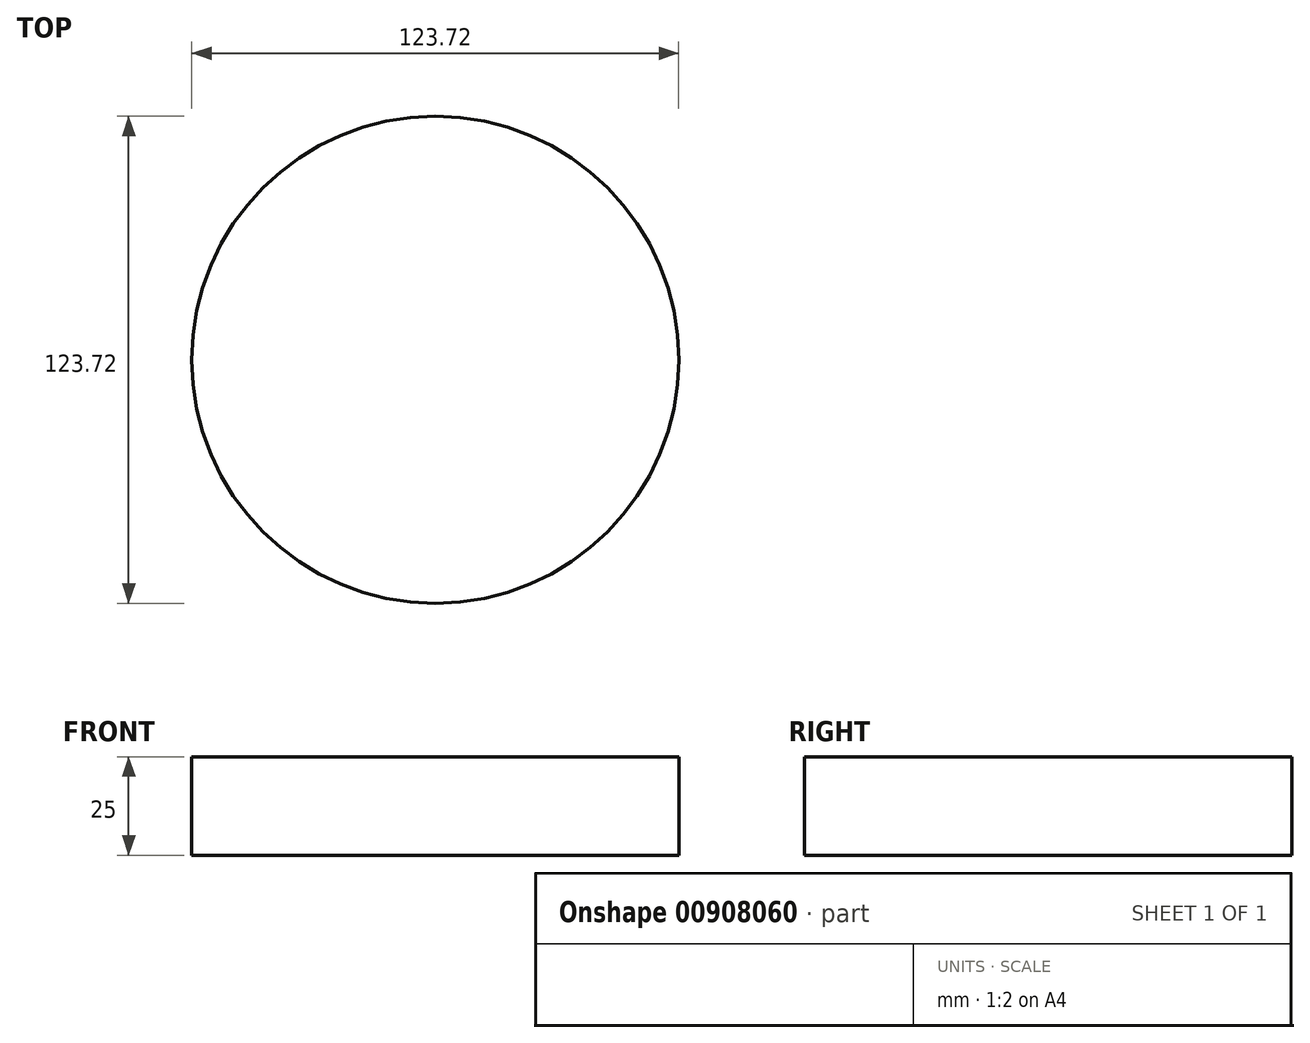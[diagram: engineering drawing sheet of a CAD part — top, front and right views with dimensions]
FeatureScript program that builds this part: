
annotation { "Feature Type Name" : "Feature", "Feature Type Description" : "" }
export const myFeature = defineFeature(function(context is Context, id is Id, definition is map)
    precondition{}
    {
        {
            var Q0;
            Q0=qCreatedBy(makeId("Top.planeOp"),FACE);
            var sketch = newSketch(context, id + "F0", { "sketchPlane" : qUnion([Q0])});
            skCircle(sketch, "E0", {"center": v(0, 0) * mm, "radius": 61.86 * mm});
            skSolve(sketch);
        }
        {
            var Q0;
            Q0=makeQuery(id+"F0.imprint","IMPRINT",FACE,{"disambiguationData":[TD([[makeQuery(id+"F0.imprint","IMPRINT",EDGE,{"derivedFrom":sQuery(id+"F0.wireOp",EDGE,"E0")}),1.0]])]});
            extrude(context, id + "F1", {"entities" : qUnion([Q0]), "depth" : 25 * mm, "offsetDistance" : 25 * mm});
        }
    });
